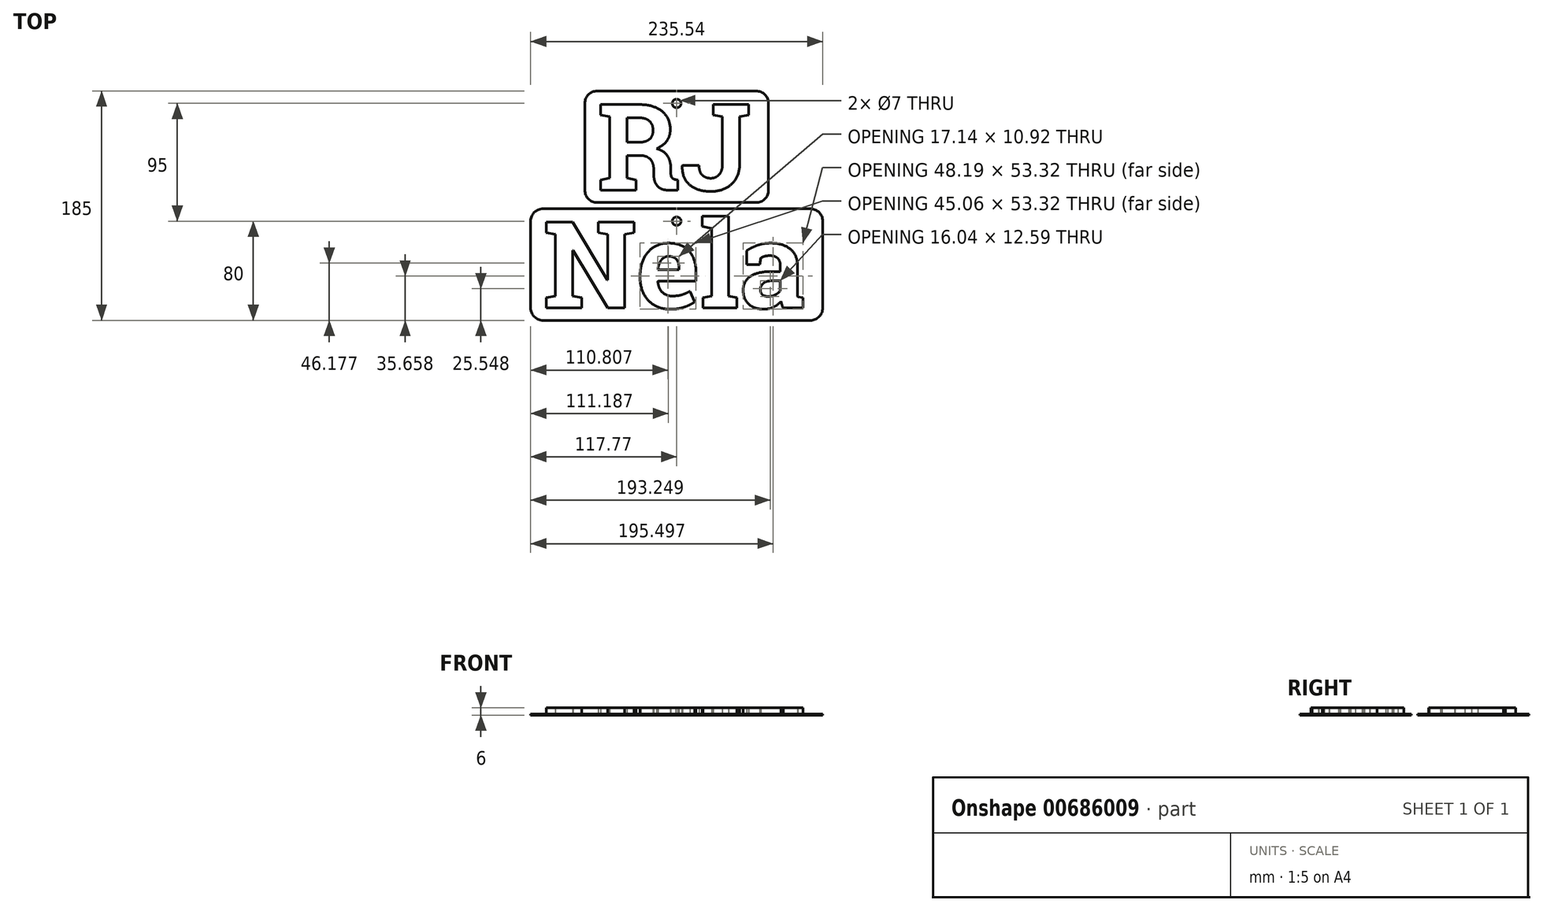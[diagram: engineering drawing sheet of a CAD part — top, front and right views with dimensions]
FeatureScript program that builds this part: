
annotation { "Feature Type Name" : "Feature", "Feature Type Description" : "" }
export const myFeature = defineFeature(function(context is Context, id is Id, definition is map)
    precondition{}
    {
        {
            var Q0;
            Q0=qCreatedBy(makeId("Top.planeOp"),FACE);
            var sketch = newSketch(context, id + "F0", { "sketchPlane" : qUnion([Q0])});
            skText(sketch, "E0", { "text": "RJ", "fontName": "RobotoSlab-Bold.ttf"});
            skText(sketch, "E1", { "text": "Nela", "fontName": "RobotoSlab-Bold.ttf"});
            skLineSegment(sketch, "E2.bottom", {"start": v(-74.05, 92.5) * mm, "end": v(74.05, 92.5) * mm});
            skLineSegment(sketch, "E2.top", {"start": v(-74.05, 2.5) * mm, "end": v(74.05, 2.5) * mm});
            skLineSegment(sketch, "E2.left", {"start": v(-74.05, 92.5) * mm, "end": v(-74.05, 2.5) * mm});
            skLineSegment(sketch, "E2.right", {"start": v(74.05, 92.5) * mm, "end": v(74.05, 2.5) * mm});
            skLineSegment(sketch, "E3.bottom", {"start": v(-117.77, -2.5) * mm, "end": v(117.77, -2.5) * mm});
            skLineSegment(sketch, "E3.top", {"start": v(-117.77, -92.5) * mm, "end": v(117.77, -92.5) * mm});
            skLineSegment(sketch, "E3.left", {"start": v(-117.77, -2.5) * mm, "end": v(-117.77, -92.5) * mm});
            skLineSegment(sketch, "E3.right", {"start": v(117.77, -2.5) * mm, "end": v(117.77, -92.5) * mm});
            skLineSegment(sketch, "E4", {"start": v(0, 2.5) * mm, "end": v(0, -2.5) * mm, "construction": true});
            skPoint(sketch, "E5", {"position": v(0, 0) * mm});
            skCircle(sketch, "E6", {"center": v(0, 82.5) * mm, "radius": 3.5 * mm});
            skCircle(sketch, "E7", {"center": v(0, -12.5) * mm, "radius": 3.5 * mm});
            const initialGuessF0  = {"E0": [-0.06405, 0.0125, 1, 0, 0.07], "E1": [-0.10777, -0.0825, 1, 0, 0.07]};
            skSetInitialGuess(sketch, initialGuessF0);
            skSolve(sketch);
        }
        {
            var Q0;
            Q0=makeQuery(id+"F0.imprint","IMPRINT",FACE,{"disambiguationData":[TD([[makeQuery(id+"F0.imprint","IMPRINT",EDGE,{"derivedFrom":sQuery(id+"F0.wireOp",EDGE,"E0.sketch_text.stroke-0")}),1.0]])]});
            var Q1;
            Q1=makeQuery(id+"F0.imprint","IMPRINT",FACE,{"disambiguationData":[TD([[makeQuery(id+"F0.imprint","IMPRINT",EDGE,{"derivedFrom":sQuery(id+"F0.wireOp",EDGE,"E0.sketch_text.stroke-42")}),1.0]])]});
            var Q2;
            Q2=makeQuery(id+"F0.imprint","IMPRINT",FACE,{"disambiguationData":[TD([[makeQuery(id+"F0.imprint","IMPRINT",EDGE,{"derivedFrom":sQuery(id+"F0.wireOp",EDGE,"E0.sketch_text.stroke-53")}),-1.0]])]});
            var Q3;
            Q3=makeQuery(id+"F0.imprint","IMPRINT",FACE,{"disambiguationData":[TD([[makeQuery(id+"F0.imprint","IMPRINT",EDGE,{"derivedFrom":sQuery(id+"F0.wireOp",EDGE,"E1.sketch_text.stroke-0")}),-1.0]])]});
            var Q4;
            Q4=makeQuery(id+"F0.imprint","IMPRINT",FACE,{"disambiguationData":[TD([[makeQuery(id+"F0.imprint","IMPRINT",EDGE,{"derivedFrom":sQuery(id+"F0.wireOp",EDGE,"E1.sketch_text.stroke-40")}),1.0]])]});
            var Q5;
            Q5=makeQuery(id+"F0.imprint","IMPRINT",FACE,{"disambiguationData":[TD([[makeQuery(id+"F0.imprint","IMPRINT",EDGE,{"derivedFrom":sQuery(id+"F0.wireOp",EDGE,"E1.sketch_text.stroke-74")}),-1.0]])]});
            var Q6;
            Q6=makeQuery(id+"F0.imprint","IMPRINT",FACE,{"disambiguationData":[TD([[makeQuery(id+"F0.imprint","IMPRINT",EDGE,{"derivedFrom":sQuery(id+"F0.wireOp",EDGE,"E1.sketch_text.stroke-96")}),1.0]])]});
            var Q7;
            Q7=makeQuery(id+"F0.imprint","IMPRINT",FACE,{"disambiguationData":[TD([[makeQuery(id+"F0.imprint","IMPRINT",EDGE,{"derivedFrom":sQuery(id+"F0.wireOp",EDGE,"E0.sketch_text.stroke-0")}),-1.0]])]});
            var Q8;
            Q8=makeQuery(id+"F0.imprint","IMPRINT",FACE,{"disambiguationData":[TD([[makeQuery(id+"F0.imprint","IMPRINT",EDGE,{"derivedFrom":sQuery(id+"F0.wireOp",EDGE,"E1.sketch_text.stroke-40")}),-1.0]])]});
            var Q9;
            Q9=makeQuery(id+"F0.imprint","IMPRINT",FACE,{"disambiguationData":[TD([[makeQuery(id+"F0.imprint","IMPRINT",EDGE,{"derivedFrom":sQuery(id+"F0.wireOp",EDGE,"E1.sketch_text.stroke-96")}),-1.0]])]});
            var Q10;
            Q10=makeQuery(id+"F0.imprint","IMPRINT",FACE,{"disambiguationData":[TD([[makeQuery(id+"F0.imprint","IMPRINT",EDGE,{"derivedFrom":sQuery(id+"F0.wireOp",EDGE,"E1.sketch_text.stroke-0")}),1.0]])]});
            var Q11;
            Q11=makeQuery(id+"F0.imprint","IMPRINT",FACE,{"disambiguationData":[TD([[makeQuery(id+"F0.imprint","IMPRINT",EDGE,{"derivedFrom":sQuery(id+"F0.wireOp",EDGE,"E0.sketch_text.stroke-29")}),1.0]])]});
            var Q12;
            Q12=makeQuery(id+"F0.imprint","IMPRINT",FACE,{"disambiguationData":[TD([[makeQuery(id+"F0.imprint","IMPRINT",EDGE,{"derivedFrom":sQuery(id+"F0.wireOp",EDGE,"E1.sketch_text.stroke-48")}),-1.0]])]});
            var Q13;
            Q13=makeQuery(id+"F0.imprint","IMPRINT",FACE,{"disambiguationData":[TD([[makeQuery(id+"F0.imprint","IMPRINT",EDGE,{"derivedFrom":sQuery(id+"F0.wireOp",EDGE,"E1.sketch_text.stroke-85")}),1.0]])]});
            var Q14;
            Q14=makeQuery(id+"F0.imprint","IMPRINT",FACE,{"disambiguationData":[TD([[makeQuery(id+"F0.imprint","IMPRINT",EDGE,{"derivedFrom":sQuery(id+"F0.wireOp",EDGE,"E1.sketch_text.stroke-41")}),1.0]])]});
            extrude(context, id + "F1", {"entities" : qUnion([Q0, Q1, Q2, Q3, Q4, Q5, Q6, Q7, Q8, Q9, Q10, Q11, Q12, Q13, Q14]), "oppositeDirection" : true, "depth" : 1 * mm, "offsetDistance" : 25 * mm});
        }
        {
            var Q0;
            Q0=makeQuery(id+"F0.imprint","IMPRINT",FACE,{"disambiguationData":[TD([[makeQuery(id+"F0.imprint","IMPRINT",EDGE,{"derivedFrom":sQuery(id+"F0.wireOp",EDGE,"E0.sketch_text.stroke-0")}),-1.0]])]});
            var Q1;
            Q1=makeQuery(id+"F0.imprint","IMPRINT",FACE,{"disambiguationData":[TD([[makeQuery(id+"F0.imprint","IMPRINT",EDGE,{"derivedFrom":sQuery(id+"F0.wireOp",EDGE,"E0.sketch_text.stroke-53")}),-1.0]])]});
            extrude(context, id + "F2", {"entities" : qUnion([Q0, Q1]), "operationType" : NewBodyOperationType.ADD, "depth" : 5 * mm, "offsetDistance" : 25 * mm});
        }
        {
            var Q0;
            Q0=makeQuery(id+"F0.imprint","IMPRINT",FACE,{"disambiguationData":[TD([[makeQuery(id+"F0.imprint","IMPRINT",EDGE,{"derivedFrom":sQuery(id+"F0.wireOp",EDGE,"E1.sketch_text.stroke-0")}),-1.0]])]});
            var Q1;
            Q1=makeQuery(id+"F0.imprint","IMPRINT",FACE,{"disambiguationData":[TD([[makeQuery(id+"F0.imprint","IMPRINT",EDGE,{"derivedFrom":sQuery(id+"F0.wireOp",EDGE,"E1.sketch_text.stroke-24")}),-1.0]])]});
            var Q2;
            Q2=makeQuery(id+"F0.imprint","IMPRINT",FACE,{"disambiguationData":[TD([[makeQuery(id+"F0.imprint","IMPRINT",EDGE,{"derivedFrom":sQuery(id+"F0.wireOp",EDGE,"E1.sketch_text.stroke-48")}),-1.0]])]});
            var Q3;
            Q3=makeQuery(id+"F0.imprint","IMPRINT",FACE,{"disambiguationData":[TD([[makeQuery(id+"F0.imprint","IMPRINT",EDGE,{"derivedFrom":sQuery(id+"F0.wireOp",EDGE,"E1.sketch_text.stroke-58")}),-1.0]])]});
            var Q4;
            Q4=makeQuery(id+"F2.opExtrude","CAP_FACE",FACE,{"disambiguationData":[OSD([sQuery(id+"F0.wireOp",EDGE,"E0.sketch_text.stroke-53"),sQuery(id+"F0.wireOp",EDGE,"E0.sketch_text.stroke-54"),sQuery(id+"F0.wireOp",EDGE,"E0.sketch_text.stroke-55"),sQuery(id+"F0.wireOp",EDGE,"E0.sketch_text.stroke-56"),sQuery(id+"F0.wireOp",EDGE,"E0.sketch_text.stroke-57"),sQuery(id+"F0.wireOp",EDGE,"E0.sketch_text.stroke-58"),sQuery(id+"F0.wireOp",EDGE,"E0.sketch_text.stroke-59"),sQuery(id+"F0.wireOp",EDGE,"E0.sketch_text.stroke-60"),sQuery(id+"F0.wireOp",EDGE,"E0.sketch_text.stroke-61"),sQuery(id+"F0.wireOp",EDGE,"E0.sketch_text.stroke-62"),sQuery(id+"F0.wireOp",EDGE,"E0.sketch_text.stroke-63"),sQuery(id+"F0.wireOp",EDGE,"E0.sketch_text.stroke-64"),sQuery(id+"F0.wireOp",EDGE,"E0.sketch_text.stroke-65"),sQuery(id+"F0.wireOp",EDGE,"E0.sketch_text.stroke-66"),sQuery(id+"F0.wireOp",EDGE,"E0.sketch_text.stroke-67"),sQuery(id+"F0.wireOp",EDGE,"E0.sketch_text.stroke-68"),sQuery(id+"F0.wireOp",EDGE,"E0.sketch_text.stroke-69"),sQuery(id+"F0.wireOp",EDGE,"E0.sketch_text.stroke-70"),sQuery(id+"F0.wireOp",EDGE,"E0.sketch_text.stroke-71"),sQuery(id+"F0.wireOp",EDGE,"E0.sketch_text.stroke-72"),sQuery(id+"F0.wireOp",EDGE,"E0.sketch_text.stroke-73"),sQuery(id+"F0.wireOp",EDGE,"E0.sketch_text.stroke-74"),sQuery(id+"F0.wireOp",EDGE,"E0.sketch_text.stroke-75"),sQuery(id+"F0.wireOp",EDGE,"E0.sketch_text.stroke-76"),sQuery(id+"F0.wireOp",EDGE,"E0.sketch_text.stroke-77"),sQuery(id+"F0.wireOp",EDGE,"E0.sketch_text.stroke-78"),sQuery(id+"F0.wireOp",EDGE,"E0.sketch_text.stroke-79"),sQuery(id+"F0.wireOp",EDGE,"E0.sketch_text.stroke-80")])],"isStart":false});
            extrude(context, id + "F3", {"entities" : qUnion([Q0, Q1, Q2, Q3]), "operationType" : NewBodyOperationType.ADD, "endBound" : BoundingType.UP_TO_SURFACE, "depth" : 25 * mm, "endBoundEntityFace" : qUnion([Q4]), "offsetDistance" : 25 * mm});
        }
        {
            var Q0;
            Q0=makeQuery(id+"F1.opExtrude","SWEPT_EDGE",EDGE,{"disambiguationData":[OSD([sQuery(id+"F0.wireOp",EDGE,"E2.bottom"),sQuery(id+"F0.wireOp",EDGE,"E2.left")])]});
            var Q1;
            Q1=makeQuery(id+"F1.opExtrude","SWEPT_EDGE",EDGE,{"disambiguationData":[OSD([sQuery(id+"F0.wireOp",EDGE,"E2.bottom"),sQuery(id+"F0.wireOp",EDGE,"E2.right")])]});
            var Q2;
            Q2=makeQuery(id+"F1.opExtrude","SWEPT_EDGE",EDGE,{"disambiguationData":[OSD([sQuery(id+"F0.wireOp",EDGE,"E2.top"),sQuery(id+"F0.wireOp",EDGE,"E2.right")])]});
            var Q3;
            Q3=makeQuery(id+"F1.opExtrude","SWEPT_EDGE",EDGE,{"disambiguationData":[OSD([sQuery(id+"F0.wireOp",EDGE,"E3.bottom"),sQuery(id+"F0.wireOp",EDGE,"E3.right")])]});
            var Q4;
            Q4=makeQuery(id+"F1.opExtrude","SWEPT_EDGE",EDGE,{"disambiguationData":[OSD([sQuery(id+"F0.wireOp",EDGE,"E3.top"),sQuery(id+"F0.wireOp",EDGE,"E3.right")])]});
            var Q5;
            Q5=makeQuery(id+"F1.opExtrude","SWEPT_EDGE",EDGE,{"disambiguationData":[OSD([sQuery(id+"F0.wireOp",EDGE,"E3.top"),sQuery(id+"F0.wireOp",EDGE,"E3.left")])]});
            var Q6;
            Q6=makeQuery(id+"F1.opExtrude","SWEPT_EDGE",EDGE,{"disambiguationData":[OSD([sQuery(id+"F0.wireOp",EDGE,"E3.bottom"),sQuery(id+"F0.wireOp",EDGE,"E3.left")])]});
            var Q7;
            Q7=makeQuery(id+"F1.opExtrude","SWEPT_EDGE",EDGE,{"disambiguationData":[OSD([sQuery(id+"F0.wireOp",EDGE,"E2.top"),sQuery(id+"F0.wireOp",EDGE,"E2.left")])]});
            fillet(context, id + "F4", {"entities" : qUnion([Q0, Q1, Q2, Q3, Q4, Q5, Q6, Q7]), "radius" : 10 * mm, "tangentPropagation" : true, "allowEdgeOverflow" : false});
        }
    });
